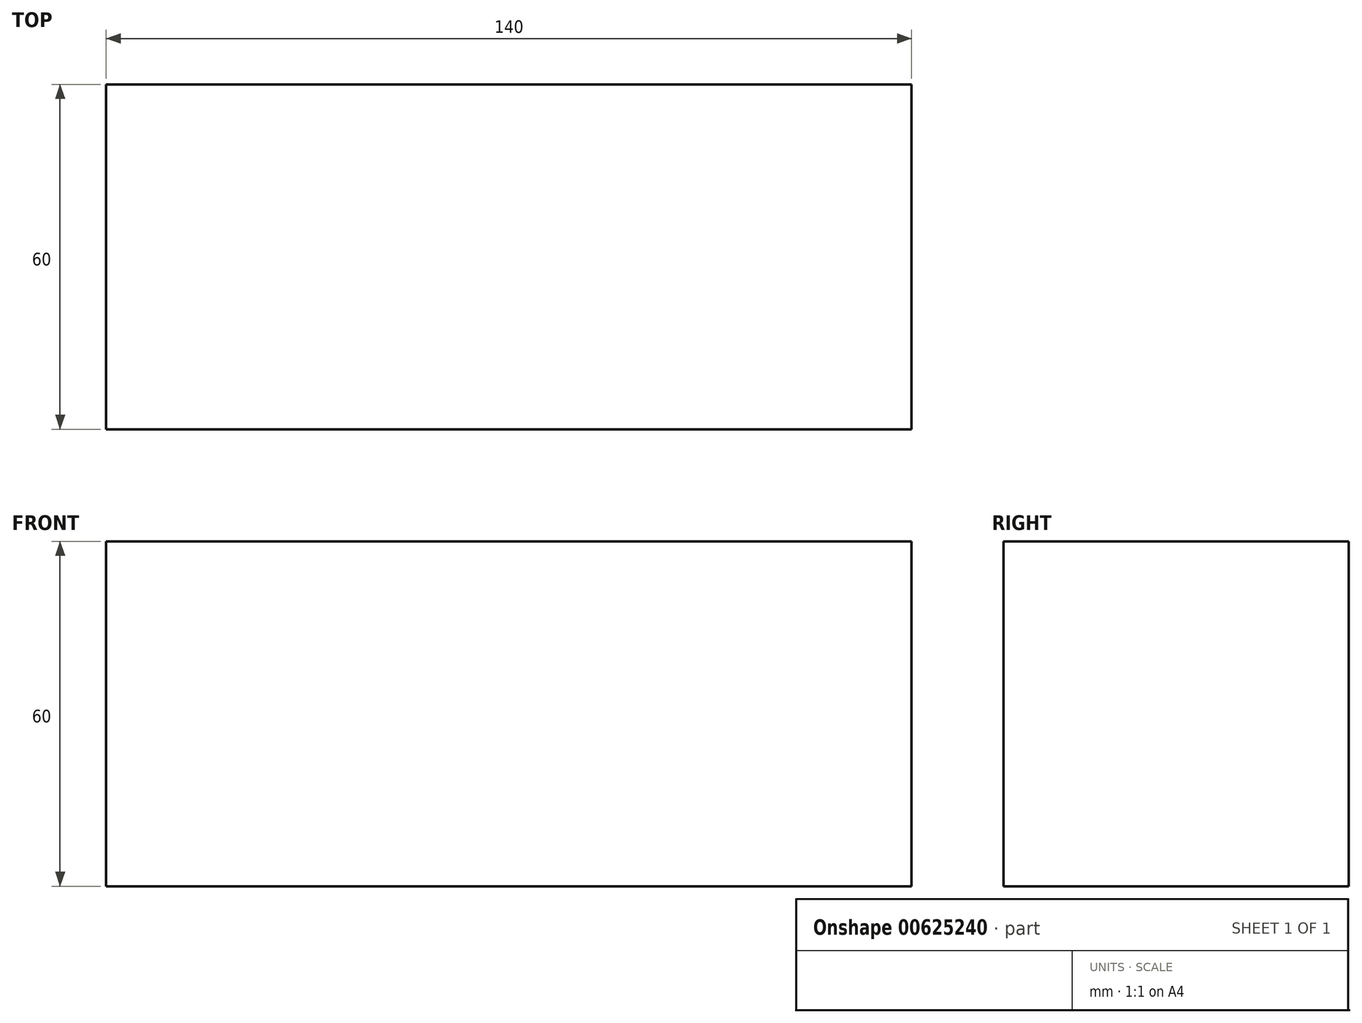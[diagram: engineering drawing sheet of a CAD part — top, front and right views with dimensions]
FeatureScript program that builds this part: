
annotation { "Feature Type Name" : "Feature", "Feature Type Description" : "" }
export const myFeature = defineFeature(function(context is Context, id is Id, definition is map)
    precondition{}
    {
        {
            var Q0;
            Q0=qCreatedBy(makeId("Top.planeOp"),FACE);
            var sketch = newSketch(context, id + "F0", { "sketchPlane" : qUnion([Q0])});
            skLineSegment(sketch, "E0.bottom", {"start": v(70, -30) * mm, "end": v(-70, -30) * mm});
            skLineSegment(sketch, "E0.top", {"start": v(70, 30) * mm, "end": v(-70, 30) * mm});
            skLineSegment(sketch, "E0.left", {"start": v(70, -30) * mm, "end": v(70, 30) * mm});
            skLineSegment(sketch, "E0.right", {"start": v(-70, -30) * mm, "end": v(-70, 30) * mm});
            skPoint(sketch, "E0.middle", {"position": v(0, 0) * mm});
            skSolve(sketch);
        }
        {
            var Q0;
            Q0 = qSketchRegion(id + "F0", true);
            extrude(context, id + "F1", {"entities" : qUnion([Q0]), "depth" : 60 * mm, "offsetDistance" : 25 * mm});
        }
    });
